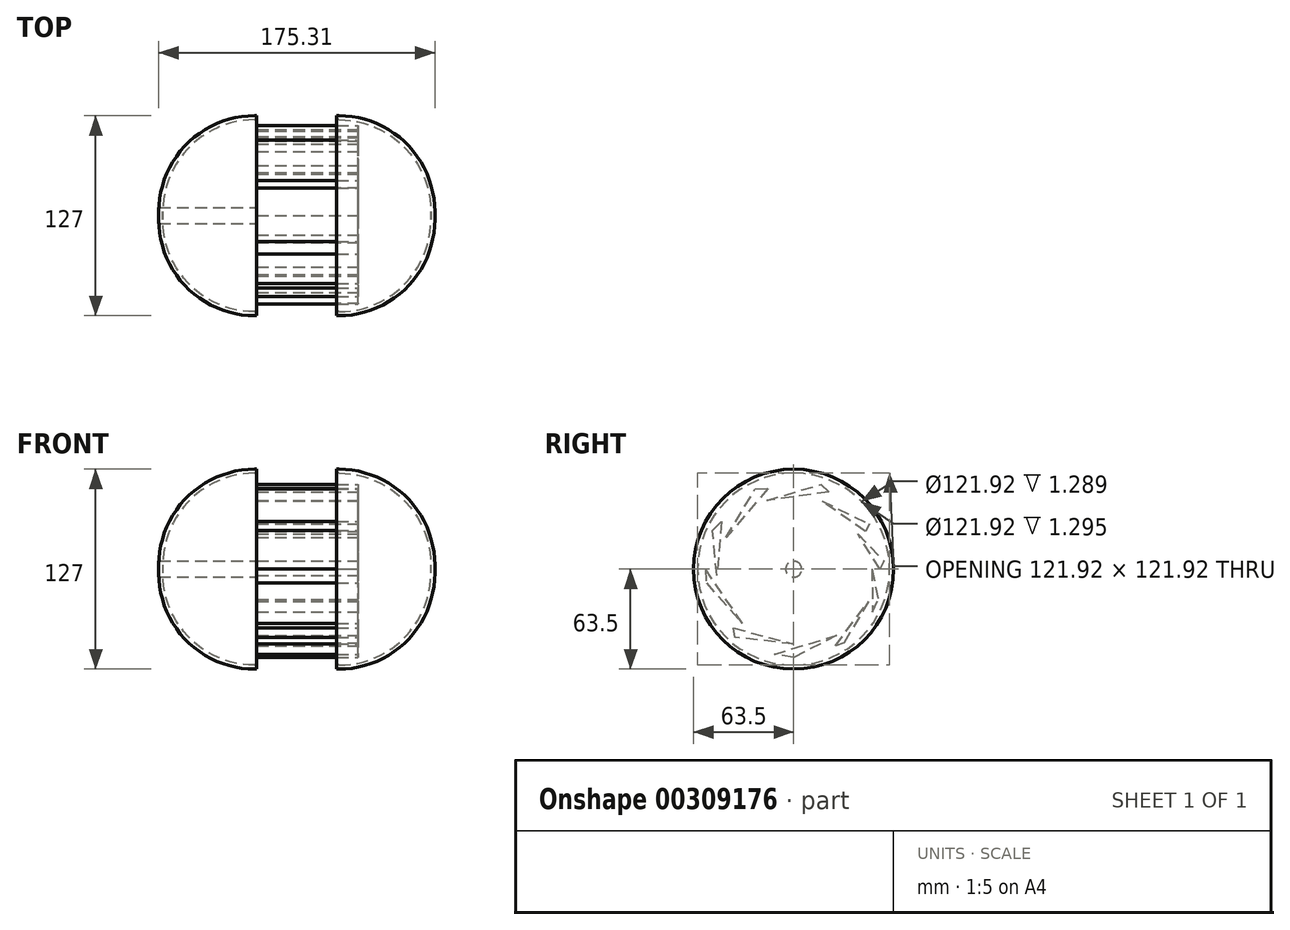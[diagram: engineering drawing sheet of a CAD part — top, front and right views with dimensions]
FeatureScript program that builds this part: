
annotation { "Feature Type Name" : "Feature", "Feature Type Description" : "" }
export const myFeature = defineFeature(function(context is Context, id is Id, definition is map)
    precondition{}
    {
        {
            var Q0;
            Q0=qCreatedBy(makeId("Right.planeOp"),FACE);
            var sketch = newSketch(context, id + "F0", { "sketchPlane" : qUnion([Q0])});
            skCircle(sketch, "E0", {"center": v(0, 0) * mm, "radius": 63.5 * mm});
            skSolve(sketch);
        }
        {
            var Q0;
            Q0=makeQuery(id+"F0.imprint","IMPRINT",FACE,{"disambiguationData":[TD([[makeQuery(id+"F0.imprint","IMPRINT",EDGE,{"derivedFrom":sQuery(id+"F0.wireOp",EDGE,"E0")}),1.0]])]});
            extrude(context, id + "F1", {"entities" : qUnion([Q0]), "depth" : 62.25 * mm});
        }
        {
            var Q0;
            Q0=makeQuery(id+"F1.opExtrude","CAP_FACE",FACE,{"disambiguationData":[OSD([sQuery(id+"F0.wireOp",EDGE,"E0")])],"isStart":false});
            fillet(context, id + "F2", {"entities" : qUnion([Q0]), "radius" : 60.96 * mm, "tangentPropagation" : true, "allowEdgeOverflow" : false});
        }
        {
            var Q0;
            Q0=makeQuery(id+"F1.opExtrude","CAP_FACE",FACE,{"disambiguationData":[OSD([sQuery(id+"F0.wireOp",EDGE,"E0")])],"isStart":true});
            shell(context, id + "F3", {"entities" : qUnion([Q0]), "thickness" : 2.54 * mm});
        }
        {
            var Q0;
            Q0=qCreatedBy(makeId("Right.planeOp"),FACE);
            var sketch = newSketch(context, id + "F4", { "sketchPlane" : qUnion([Q0])});
            skLineSegment(sketch, "E1", {"start": v(0, -56.04) * mm, "end": v(-12.28, -54.03) * mm});
            skLineSegment(sketch, "E2", {"start": v(-12.28, -54.03) * mm, "end": v(27.32, -42.1) * mm});
            skLineSegment(sketch, "E3", {"start": v(27.32, -42.1) * mm, "end": v(0, -56.04) * mm});
            skLineSegment(sketch, "E4", {"start": v(31.88, -46.96) * mm, "end": v(26.45, -48.8) * mm});
            skLineSegment(sketch, "E5", {"start": v(26.45, -48.8) * mm, "end": v(47.54, -20.5) * mm});
            skLineSegment(sketch, "E6", {"start": v(47.54, -20.5) * mm, "end": v(31.88, -46.96) * mm});
            skLineSegment(sketch, "E7", {"start": v(57.24, 5.09) * mm, "end": v(54.8, 0) * mm});
            skLineSegment(sketch, "E8", {"start": v(54.8, 0) * mm, "end": v(40.7, 22.26) * mm});
            skLineSegment(sketch, "E9", {"start": v(40.7, 22.26) * mm, "end": v(57.24, 5.09) * mm});
            skLineSegment(sketch, "E10", {"start": v(48.2, 28.62) * mm, "end": v(45.5, 23.93) * mm});
            skLineSegment(sketch, "E11", {"start": v(45.5, 23.93) * mm, "end": v(17.88, 43.35) * mm});
            skLineSegment(sketch, "E12", {"start": v(17.88, 43.35) * mm, "end": v(48.2, 28.62) * mm});
            skLineSegment(sketch, "E13", {"start": v(-17, 43.65) * mm, "end": v(17.47, 53.84) * mm});
            skLineSegment(sketch, "E14", {"start": v(50.17, -27.12) * mm, "end": v(53.75, -19.3) * mm});
            skLineSegment(sketch, "E15", {"start": v(49.71, 0) * mm, "end": v(50.17, -27.12) * mm});
            skLineSegment(sketch, "E16", {"start": v(49.71, 0) * mm, "end": v(53.75, -19.3) * mm});
            skLineSegment(sketch, "E17", {"start": v(-24.45, 50.84) * mm, "end": v(-16.35, 51.25) * mm});
            skLineSegment(sketch, "E18", {"start": v(-16.35, 51.25) * mm, "end": v(-42.93, 20.08) * mm});
            skLineSegment(sketch, "E19", {"start": v(-42.93, 20.08) * mm, "end": v(-24.45, 50.84) * mm});
            skLineSegment(sketch, "E20", {"start": v(-51.43, 24.68) * mm, "end": v(-45.8, 30.23) * mm});
            skLineSegment(sketch, "E21", {"start": v(-45.8, 30.23) * mm, "end": v(-48.78, -3.87) * mm});
            skLineSegment(sketch, "E22", {"start": v(-48.78, -3.87) * mm, "end": v(-51.43, 24.68) * mm});
            skLineSegment(sketch, "E23", {"start": v(-56.02, 0) * mm, "end": v(-55.43, -8.8) * mm});
            skLineSegment(sketch, "E24", {"start": v(-55.43, -8.8) * mm, "end": v(-32.43, -34.53) * mm});
            skLineSegment(sketch, "E25", {"start": v(-32.43, -34.53) * mm, "end": v(-56.02, 0) * mm});
            skLineSegment(sketch, "E26", {"start": v(-37.23, -43.3) * mm, "end": v(-38.28, -37.47) * mm});
            skLineSegment(sketch, "E27", {"start": v(-38.28, -37.47) * mm, "end": v(0, -47.56) * mm});
            skLineSegment(sketch, "E28", {"start": v(0, -47.56) * mm, "end": v(-37.23, -43.3) * mm});
            skLineSegment(sketch, "E29", {"start": v(17.47, 53.84) * mm, "end": v(22.3, 49.16) * mm});
            skLineSegment(sketch, "E30", {"start": v(22.3, 49.16) * mm, "end": v(-17, 43.65) * mm});
            skSolve(sketch);
        }
        {
            var Q0;
            Q0=qSketchRegion(id+"F4",true);
            extrude(context, id + "F5", {"entities" : qUnion([Q0]), "oppositeDirection" : true, "depth" : 50.8 * mm, "hasSecondDirection" : true, "secondDirectionOppositeDirection" : false, "secondDirectionDepth" : 13.65 * mm});
        }
        {
            var Q0;
            Q0=makeQuery(id+"F5.opExtrude","CAP_FACE",FACE,{"disambiguationData":[OSD([sQuery(id+"F4.wireOp",EDGE,"E20"),sQuery(id+"F4.wireOp",EDGE,"E21"),sQuery(id+"F4.wireOp",EDGE,"E22")])],"isStart":false});
            var sketch = newSketch(context, id + "F6", { "sketchPlane" : qUnion([Q0])});
            skCircle(sketch, "E31", {"center": v(0, 0) * mm, "radius": 63.5 * mm});
            skSolve(sketch);
        }
        {
            var Q0;
            Q0=qSketchRegion(id+"F6",true);
            extrude(context, id + "F7", {"entities" : qUnion([Q0]), "depth" : 62.26 * mm});
        }
        {
            var Q0;
            Q0=makeQuery(id+"F7.opExtrude","CAP_EDGE",EDGE,{"disambiguationData":[OSD([sQuery(id+"F6.wireOp",EDGE,"E31")])],"isStart":false});
            fillet(context, id + "F8", {"entities" : qUnion([Q0]), "radius" : 60.96 * mm, "tangentPropagation" : true, "allowEdgeOverflow" : false});
        }
        {
            var Q0;
            Q0=makeQuery(id+"F7.opExtrude","CAP_FACE",FACE,{"disambiguationData":[OSD([sQuery(id+"F6.wireOp",EDGE,"E31")])],"isStart":true});
            shell(context, id + "F9", {"entities" : qUnion([Q0]), "thickness" : 2.54 * mm});
        }
        {
            var Q0;
            Q0=makeQuery(id+"F5.opExtrude","CAP_FACE",FACE,{"disambiguationData":[OSD([sQuery(id+"F4.wireOp",EDGE,"E17"),sQuery(id+"F4.wireOp",EDGE,"E18"),sQuery(id+"F4.wireOp",EDGE,"E19")])],"isStart":false});
            var sketch = newSketch(context, id + "F10", { "sketchPlane" : qUnion([Q0])});
            skLineSegment(sketch, "E32", {"start": v(0, 0) * mm, "end": v(29.58, 0) * mm});
            skLineSegment(sketch, "E33", {"start": v(29.58, 0) * mm, "end": v(-29.58, 0) * mm});
            skCircle(sketch, "E34", {"center": v(0, 0) * mm, "radius": 5.08 * mm});
            skSolve(sketch);
        }
        {
            var Q0;
            Q0=qSketchRegion(id+"F10",true);
            extrude(context, id + "F11", {"entities" : qUnion([Q0]), "depth" : 62.23 * mm});
        }
    });
